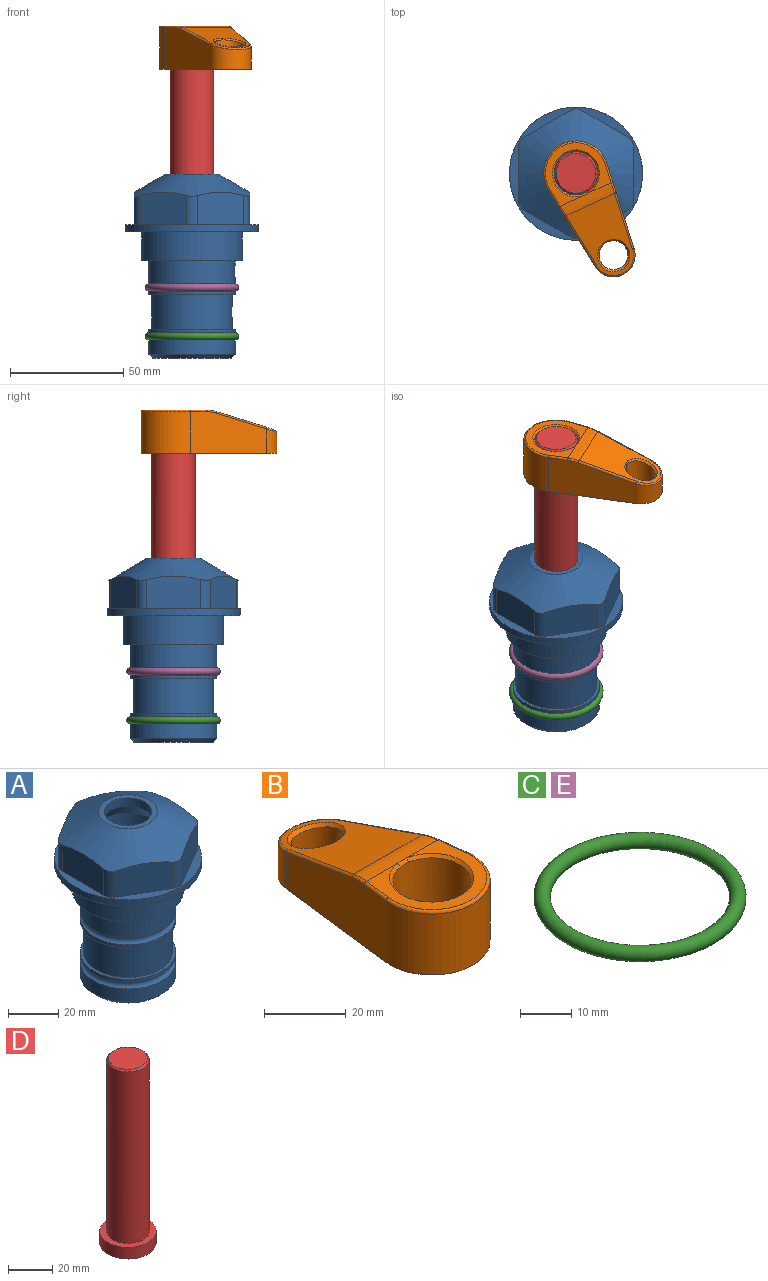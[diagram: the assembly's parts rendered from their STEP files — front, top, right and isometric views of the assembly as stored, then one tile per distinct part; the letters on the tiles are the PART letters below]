
ASSEMBLY  parts=5 mates=4
PART A: 36 faces, bbox 58.7x58.7x81 mm
  f0: cylinder r=17.78mm len=35.56mm, axis (0,0,1), area 1670.8mm2, adj f23,f24,f31
  f1: cylinder r=19.05mm len=38.1mm, axis (0,0,1), area 1191.9mm2, adj f26,f27,f30
  f2: plane 58.66x58.66mm, normal (0,0,-1), area 1150.6mm2, adj f3,f28
  f3: cylinder r=29.33mm len=58.66mm, axis (0,0,-1), area 585.1mm2, adj f2,f4
  f4: plane 58.66x58.66mm, normal (0,0,1), area 475.9mm2, adj f3,f5,f6,f7,f8,f9,f10,f11
  f5: plane 20.32x14.34mm, normal (-0.5,0.87,0), area 324.4mm2, adj f4,f15,f16,f17
  f6: plane 20.32x14.34mm, normal (0.5,0.87,0), area 324.4mm2, adj f4,f14,f15,f17
  f7: plane 23.48x14.34mm, normal (1,0,0), area 324.4mm2, adj f4,f13,f14,f17
  f8: plane 20.32x14.34mm, normal (0.5,-0.87,0), area 324.4mm2, adj f4,f12,f13,f17
  f9: plane 20.32x14.34mm, normal (-0.5,-0.87,0), area 324.4mm2, adj f4,f11,f12,f17
  f10: plane 23.48x14.34mm, normal (-1,0,0), area 324.4mm2, adj f4,f11,f16,f17
  f11: cylinder r=5.08mm len=12.85mm, axis (0,0,-1), area 67.2mm2, adj f4,f9,f10,f17
  f12: cylinder r=5.08mm len=12.85mm, axis (0,0,-1), area 67.2mm2, adj f4,f8,f9,f17
  f13: cylinder r=5.08mm len=12.85mm, axis (0,0,-1), area 67.2mm2, adj f4,f7,f8,f17
  f14: cylinder r=5.08mm len=12.85mm, axis (0,0,-1), area 67.2mm2, adj f4,f6,f7,f17
  f15: cylinder r=5.08mm len=12.85mm, axis (0,0,-1), area 67.2mm2, adj f4,f5,f6,f17
  f16: cylinder r=5.08mm len=12.85mm, axis (0,0,-1), area 67.2mm2, adj f4,f5,f10,f17
  f17: cone r=11.73mm half-angle=60deg, axis (0,0,-1), area 2071.8mm2, adj f5,f6,f7,f8,f9,f10,f11,f12
  f18: plane 23.46x23.46mm, normal (0,0,1), area 147.4mm2, adj f17,f35
  f19: plane 34.93x34.93mm, normal (0,0,-1), area 958mm2, adj f29
  f20: cylinder r=19.05mm len=38.1mm, axis (0,0,1), area 760.1mm2, adj f21,f29
  f21: torus R=19.05mm, axis (0,0,1), area 565.3mm2, adj f20,f22
  f22: cylinder r=19.05mm len=38.1mm, axis (0,0,1), area 190mm2, adj f21,f23
  f23: plane 38.1x38.1mm, normal (0,0,1), area 146.9mm2, adj f0,f22
  f24: plane 38.1x38.1mm, normal (0,0,-1), area 146.9mm2, adj f0,f25
  f25: cylinder r=19.05mm len=38.1mm, axis (0,0,1), area 190mm2, adj f24,f26
  f26: torus R=19.05mm, axis (0,0,1), area 565.3mm2, adj f1,f25
  f27: plane 44.45x44.45mm, normal (0,0,-1), area 411.7mm2, adj f1,f28
  f28: cylinder r=22.23mm len=44.45mm, axis (0,0,1), area 1773.5mm2, adj f2,f27
  f29: cone r=19.05mm half-angle=45deg, axis (0,0,1), area 257.5mm2, adj f19,f20
  f30: cylinder r=3.17mm len=6.75mm, axis (-1,0,0), area 128mm2, adj f1,f33
  f31: cylinder r=3.17mm len=6.35mm, axis (-1,0,0), area 102.5mm2, adj f0,f33
  f32: plane 25.4x25.4mm, normal (0,0,1), area 506.7mm2, adj f33
  f33: cylinder r=12.7mm len=66.42mm, axis (0,0,-1), area 5236.2mm2, adj f30,f31,f32,f34
  f34: cone r=9.53mm half-angle=30deg, axis (0,0,-1), area 443.4mm2, adj f33,f35
  f35: cylinder r=9.53mm len=19.05mm, axis (0,0,-1), area 240.9mm2, adj f18,f34
PART B: 31 faces, bbox 31.7x65.5x19.8 mm
  f0: plane 39.12x18.26mm, normal (0.99,0.12,0), area 612.2mm2, adj f1,f4,f7,f11,f13,f15
  f1: cylinder r=9.53mm len=18.91mm, axis (0,0,-1), area 296.1mm2, adj f0,f2,f7,f17
  f2: plane 39.12x18.26mm, normal (-0.99,0.12,0), area 612.2mm2, adj f1,f4,f7,f12,f14,f16
  f3: cylinder r=6.35mm len=12.7mm, axis (0,0,-1), area 362.4mm2, adj f7,f18
  f4: cylinder r=14.29mm len=28.58mm, axis (0,0,-1), area 882.2mm2, adj f0,f2,f7,f10
  f5: cylinder r=9.53mm len=19.05mm, axis (0,0,-1), area 1092.6mm2, adj f7,f19,f20
  f6: plane 26.99x23.69mm, normal (0,0,1), area 216.2mm2, adj f9,f10,f11,f12,f19
  f7: plane 63.5x28.58mm, normal (0,0,-1), area 661.8mm2, adj f0,f1,f2,f3,f4,f5,f22,f23
  f8: plane 33.52x23.6mm, normal (0,0.26,0.97), area 486mm2, adj f9,f15,f16,f17,f18
  f9: cylinder r=19.05mm len=24.72mm, axis (1,0,0), area 120.4mm2, adj f6,f8,f13,f14,f20
  f10: torus R=13.49mm, axis (0,0,1), area 59mm2, adj f4,f6,f11,f12
  f11: cylinder r=0.79mm len=8.67mm, axis (0.12,-0.99,0), area 10.8mm2, adj f0,f6,f10,f13
  f12: cylinder r=0.79mm len=8.67mm, axis (0.12,0.99,0), area 10.8mm2, adj f2,f6,f10,f14
  f13: bspline ~4.95x1.42mm, area 6.1mm2, adj f0,f9,f11,f15
  f14: bspline ~4.95x1.42mm, area 6.1mm2, adj f2,f9,f12,f16
  f15: cylinder r=0.79mm len=25.95mm, axis (0.12,-0.96,0.26), area 32.9mm2, adj f0,f8,f13,f17
  f16: cylinder r=0.79mm len=25.95mm, axis (0.12,0.96,-0.26), area 32.9mm2, adj f2,f8,f14,f17
  f17: bspline ~18.91x8.38mm, area 30mm2, adj f1,f8,f15,f16
  f18: bspline ~14.29x14.29mm, area 48.3mm2, adj f3,f8
  f19: cone r=9.53mm half-angle=45deg, axis (0,0,1), area 66.5mm2, adj f5,f6,f20
  f20: bspline ~3.22x0.96mm, area 3.5mm2, adj f5,f9,f19
  f21: plane 2.75x2.72mm, normal (0,0,-1), area 2.9mm2, adj f23,f25,f28
  f22: plane 23.05x15.88mm, normal (-0.99,-0.12,0), area 323.6mm2, adj f7,f25,f26,f27,f28,f29
  f23: plane 23.05x15.88mm, normal (0.99,-0.12,0), area 323.6mm2, adj f7,f21,f25,f27,f28,f30
  f24: cylinder r=9.53mm len=10.69mm, axis (0,0,-1), area 114.7mm2, adj f7,f27,f29,f30
  f25: cylinder r=12.7mm len=20.59mm, axis (0,0,-1), area 381.1mm2, adj f7,f21,f22,f23,f26,f28
  f26: plane 2.75x2.72mm, normal (0,0,-1), area 2.9mm2, adj f22,f25,f28
  f27: plane 19.72x18.37mm, normal (0,-0.26,-0.97), area 291.8mm2, adj f22,f23,f24,f28,f29,f30
  f28: cylinder r=15.88mm len=19.92mm, axis (1,0,0), area 54.8mm2, adj f21,f22,f23,f25,f26,f27
  f29: cylinder r=1.59mm len=11mm, axis (0,0,-1), area 34.7mm2, adj f7,f22,f24,f27
  f30: cylinder r=1.59mm len=11mm, axis (0,0,-1), area 34.7mm2, adj f7,f23,f24,f27
PART C: 1 faces, bbox 44.7x44.7x3.2 mm
  f0: torus R=19.05mm, axis (0,0,1), area 1193.9mm2
PART D: 6 faces, bbox 25.4x25.4x101.6 mm
  f0: plane 17.46x17.46mm, normal (0,0,1), area 239.5mm2, adj f5
  f1: plane 25.4x25.4mm, normal (0,0,-1), area 506.7mm2, adj f2
  f2: cylinder r=12.7mm len=25.4mm, axis (0,0,1), area 506.7mm2, adj f1,f3
  f3: plane 25.4x25.4mm, normal (0,0,1), area 221.7mm2, adj f2,f4
  f4: cylinder r=9.53mm len=94.46mm, axis (0,0,1), area 5653mm2, adj f3,f5
  f5: cone r=8.73mm half-angle=45deg, axis (0,0,-1), area 64.4mm2, adj f0,f4
PART E: same geometry as C
PLACE A at identity fixed
PLACE B rot(axis=(0,0,-1),155.4deg) t=(0,0,27.24)mm
PLACE C t=(0,0,-21.59)mm
PLACE D rot(axis=(0,0,-1),155.4deg) t=(0,0,27.24)mm
PLACE E at identity
MATE fastened E.f0 <-> A.f0  axis (0,0,1) through (0,0,-24.51)mm
MATE fastened C.f0 <-> A.f0  axis (0,0,1) through (0,0,-46.1)mm
MATE cylindrical D.f2 <-> A.f0  axis (0,0,-1) through (0,0,-10.86)mm
MATE fastened D.f2 <-> B.f4  axis (0,0,1) through (0,0,90.74)mm
